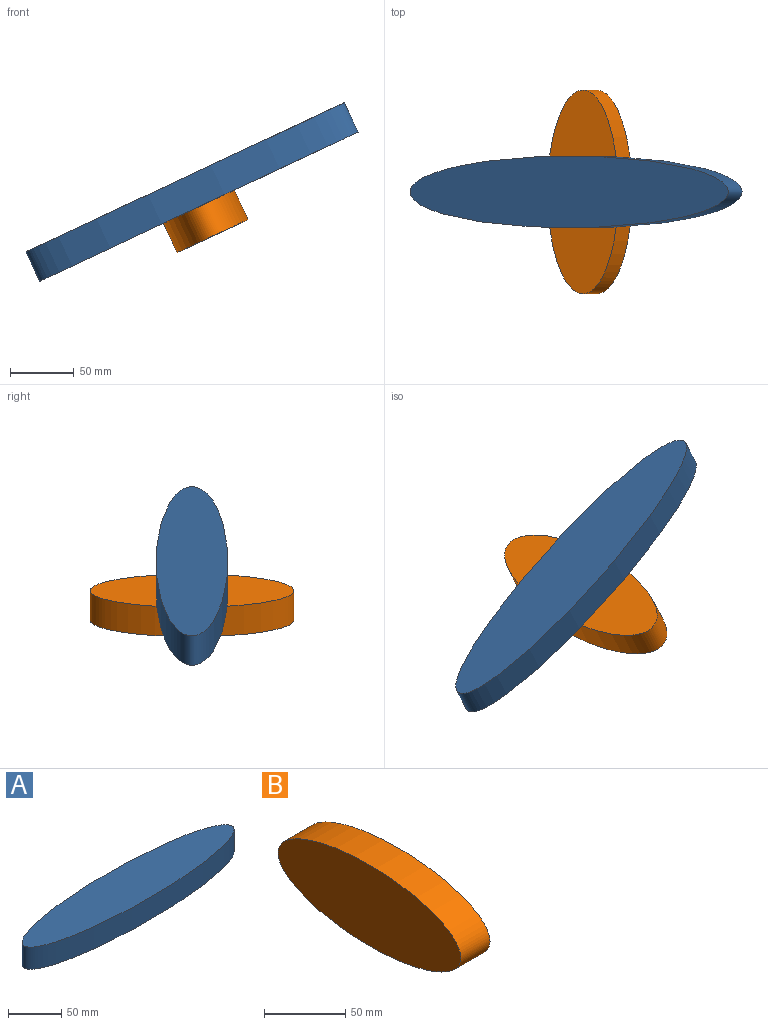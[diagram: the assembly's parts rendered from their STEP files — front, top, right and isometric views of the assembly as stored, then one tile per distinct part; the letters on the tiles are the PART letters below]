
ASSEMBLY  parts=2 mates=1
PART A: 3 faces, bbox 275x56.3x25.4 mm
  f0: extruded ~274.96x56.3mm, area 14720.1mm2, adj f1,f2
  f1: plane 274.96x56.3mm, normal (0,0,1), area 12157.8mm2, adj f0
  f2: plane 274.96x56.3mm, normal (0,0,-1), area 12157.8mm2, adj f0
PART B: 3 faces, bbox 25.4x159.4x61.4 mm
  f0: extruded ~159.4x61.35mm, area 9249.1mm2, adj f1,f2
  f1: plane 159.4x61.35mm, normal (1,0,0), area 7680.8mm2, adj f0
  f2: plane 159.4x61.35mm, normal (-1,0,0), area 7680.8mm2, adj f0
PLACE A rot(axis=(0,1,0),154.9deg) t=(-48.1,25.45,73.07)mm
PLACE B rot(axis=(0,-1,0),115.1deg) t=(-59.99,143.07,11.39)mm
MATE fastened B.f1 <-> A.f1  axis (-0.42,0,0.91) through (-37.32,25.45,50.06)mm
